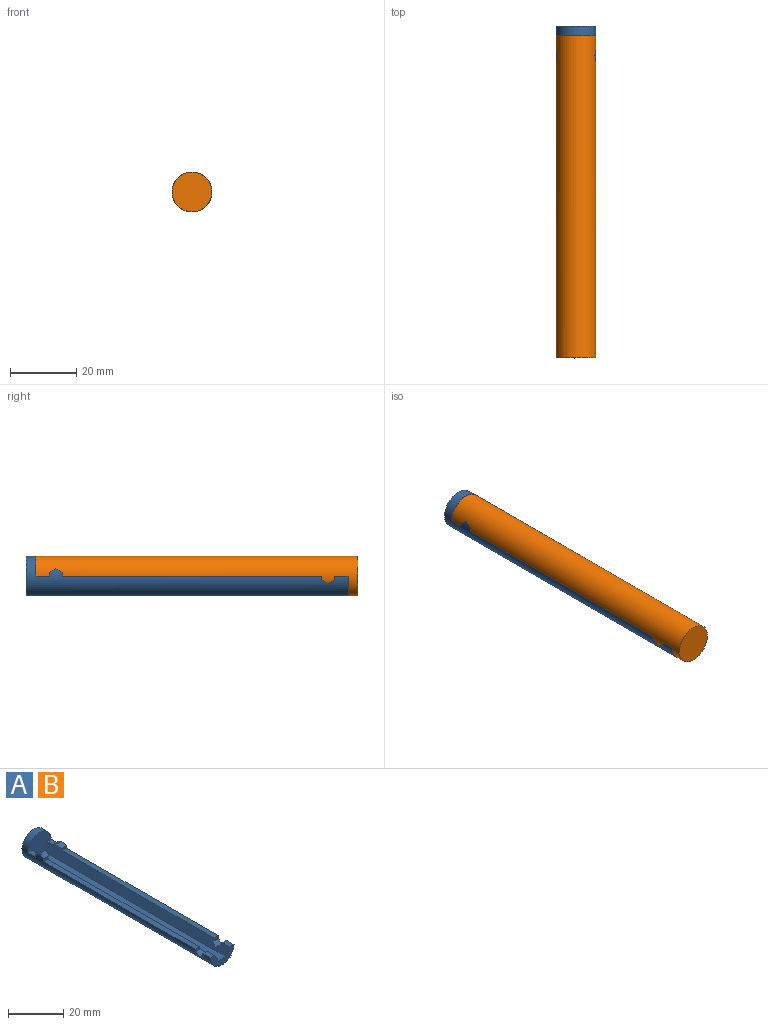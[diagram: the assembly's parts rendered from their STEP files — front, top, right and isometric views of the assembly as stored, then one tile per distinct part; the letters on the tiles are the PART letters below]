
ASSEMBLY  parts=2 mates=1
PART A: 31 faces, bbox 12x97x12 mm
  f0: plane 2.86x1.15mm, normal (0,1,0), area 2.9mm2, adj f2,f11,f15,f30
  f1: plane 2.86x1.15mm, normal (0,-1,0), area 2.9mm2, adj f3,f9,f15,f30
  f2: plane 3.41x2mm, normal (0,0.5,0.87), area 6.8mm2, adj f0,f3,f15,f30
  f3: plane 3.41x2mm, normal (0,-0.5,0.87), area 6.8mm2, adj f1,f2,f15,f30
  f4: plane 2.86x1.15mm, normal (0,1,0), area 2.9mm2, adj f6,f10,f15,f29
  f5: plane 2.86x1.15mm, normal (0,-1,0), area 2.9mm2, adj f7,f8,f15,f29
  f6: plane 3.41x2mm, normal (0,0.5,0.87), area 6.8mm2, adj f4,f7,f15,f29
  f7: plane 3.41x2mm, normal (0,-0.5,0.87), area 6.8mm2, adj f5,f6,f15,f29
  f8: plane 78x2.19mm, normal (0,0,1), area 170.8mm2, adj f5,f13,f15,f25
  f9: plane 78x2.19mm, normal (0,0,1), area 170.8mm2, adj f1,f15,f17,f24
  f10: plane 4x2.19mm, normal (0,0,1), area 8.8mm2, adj f4,f13,f15,f20
  f11: plane 4x2.19mm, normal (0,0,1), area 8.8mm2, adj f0,f15,f17,f20
  f12: plane 94x3.81mm, normal (0,0,1), area 358.2mm2, adj f13,f17,f18,f20
  f13: plane 94x3.3mm, normal (0.87,0,0.5), area 350.2mm2, adj f8,f10,f12,f14,f18,f20,f25,f26
  f14: plane 4x2.19mm, normal (0,0,1), area 8.8mm2, adj f13,f15,f18,f26
  f15: cylinder r=6mm len=97mm, axis (0,1,0), area 1885mm2, adj f0,f1,f2,f3,f4,f5,f6,f7
  f16: plane 4x2.19mm, normal (0,0,1), area 8.8mm2, adj f15,f17,f18,f23
  f17: plane 94x3.3mm, normal (-0.87,0,0.5), area 350.2mm2, adj f9,f11,f12,f16,f18,f20,f21,f22
  f18: plane 12x6mm, normal (0,-1,0), area 37.7mm2, adj f12,f13,f14,f15,f16,f17
  f19: plane 12x12mm, normal (0,1,0), area 113.1mm2, adj f15
  f20: plane 12x9.3mm, normal (0,-1,0), area 75.4mm2, adj f10,f11,f12,f13,f15,f17
  f21: plane 3.41x2mm, normal (0,-0.5,0.87), area 6.8mm2, adj f15,f17,f22,f24
  f22: plane 3.41x2mm, normal (0,0.5,0.87), area 6.8mm2, adj f15,f17,f21,f23
  f23: plane 2.86x1.15mm, normal (0,1,0), area 2.9mm2, adj f15,f16,f17,f22
  f24: plane 2.86x1.15mm, normal (0,-1,0), area 2.9mm2, adj f9,f15,f17,f21
  f25: plane 2.86x1.15mm, normal (0,-1,0), area 2.9mm2, adj f8,f13,f15,f28
  f26: plane 2.86x1.15mm, normal (0,1,0), area 2.9mm2, adj f13,f14,f15,f27
  f27: plane 3.41x2mm, normal (0,0.5,0.87), area 6.8mm2, adj f13,f15,f26,f28
  f28: plane 3.41x2mm, normal (0,-0.5,0.87), area 6.8mm2, adj f13,f15,f25,f27
  f29: plane 4x2.31mm, normal (0.87,0,-0.5), area 8mm2, adj f4,f5,f6,f7,f13
  f30: plane 4x2.31mm, normal (-0.87,0,-0.5), area 8mm2, adj f0,f1,f2,f3,f17
PART B: same geometry as A
PLACE A t=(1.96,1.94,1.57)mm
PLACE B rot(axis=(1,0,0),180deg) t=(1.96,-98.06,8.17)mm
MATE planar A.f15 <-> B.f15  axis (0,1,0) through (1.96,-95.06,4.87)mm
